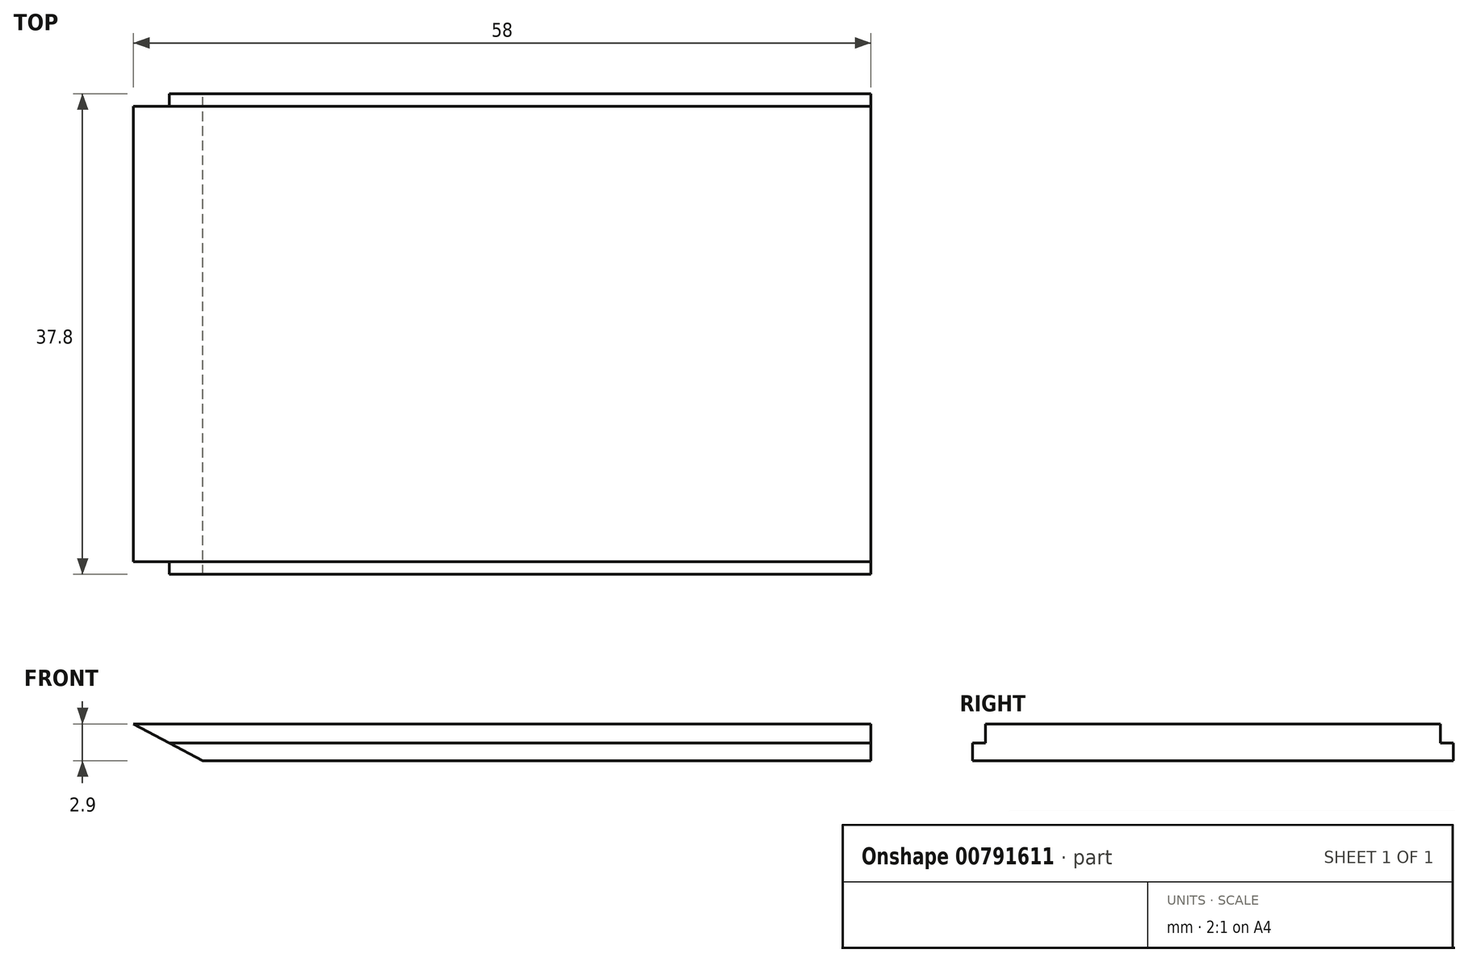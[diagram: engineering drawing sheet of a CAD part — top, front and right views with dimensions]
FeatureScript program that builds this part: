
annotation { "Feature Type Name" : "Feature", "Feature Type Description" : "" }
export const myFeature = defineFeature(function(context is Context, id is Id, definition is map)
    precondition{}
    {
        {
            var Q0;
            Q0=qCreatedBy(makeId("Top.planeOp"),FACE);
            var sketch = newSketch(context, id + "F0", { "sketchPlane" : qUnion([Q0])});
            skLineSegment(sketch, "E0.bottom", {"start": v(29, -18.9) * mm, "end": v(-29, -18.9) * mm});
            skLineSegment(sketch, "E0.top", {"start": v(29, 18.9) * mm, "end": v(-29, 18.9) * mm});
            skLineSegment(sketch, "E0.left", {"start": v(29, -18.9) * mm, "end": v(29, 18.9) * mm});
            skLineSegment(sketch, "E0.right", {"start": v(-29, -18.9) * mm, "end": v(-29, 18.9) * mm});
            skPoint(sketch, "E0.middle", {"position": v(0, 0) * mm});
            skSolve(sketch);
        }
        {
            var Q0;
            Q0 = qSketchRegion(id + "F0", true);
            extrude(context, id + "F1", {"entities" : qUnion([Q0]), "depth" : 1.4 * mm, "offsetDistance" : 25 * mm});
        }
        {
            var Q0;
            Q0=makeQuery(id+"F1.opExtrude","CAP_FACE",FACE,{"disambiguationData":[OSD([sQuery(id+"F0.wireOp",EDGE,"E0.bottom"),sQuery(id+"F0.wireOp",EDGE,"E0.top"),sQuery(id+"F0.wireOp",EDGE,"E0.left"),sQuery(id+"F0.wireOp",EDGE,"E0.right")])],"isStart":false});
            var sketch = newSketch(context, id + "F2", { "sketchPlane" : qUnion([Q0])});
            skLineSegment(sketch, "E1.bottom", {"start": v(29, -17.9) * mm, "end": v(-29, -17.9) * mm});
            skLineSegment(sketch, "E1.top", {"start": v(29, 17.9) * mm, "end": v(-29, 17.9) * mm});
            skLineSegment(sketch, "E1.left", {"start": v(29, -17.9) * mm, "end": v(29, 17.9) * mm});
            skLineSegment(sketch, "E1.right", {"start": v(-29, -17.9) * mm, "end": v(-29, 17.9) * mm});
            skPoint(sketch, "E1.middle", {"position": v(0, 0) * mm});
            skSolve(sketch);
        }
        {
            var Q0;
            Q0 = qSketchRegion(id + "F2", true);
            extrude(context, id + "F3", {"entities" : qUnion([Q0]), "operationType" : NewBodyOperationType.ADD, "depth" : 1.5 * mm, "offsetDistance" : 25 * mm});
        }
        {
            var Q0;
            Q0=makeQuery(id+"F3.opExtrude","SWEPT_FACE",FACE,{"disambiguationData":[OSD([sQuery(id+"F2.wireOp",EDGE,"E1.top")])]});
            var sketch = newSketch(context, id + "F4", { "sketchPlane" : qUnion([Q0])});
            skLineSegment(sketch, "E2", {"start": v(29, 2.9) * mm, "end": v(23.55, 2.9) * mm});
            skLineSegment(sketch, "E3", {"start": v(23.55, 2.9) * mm, "end": v(23.55, 0) * mm});
            skLineSegment(sketch, "E4", {"start": v(23.55, 0) * mm, "end": v(29, 2.9) * mm});
            skSolve(sketch);
        }
        {
            var Q0;
            Q0=makeQuery(id+"F1.opExtrude","SWEPT_FACE",FACE,{"disambiguationData":[OSD([sQuery(id+"F0.wireOp",EDGE,"E0.top")])]});
            var sketch = newSketch(context, id + "F5", { "sketchPlane" : qUnion([Q0])});
            skPoint(sketch, "E5", {"position": v(29, 2.9) * mm});
            skPoint(sketch, "E6", {"position": v(23.55, 0) * mm});
            skPoint(sketch, "E7", {"position": v(23.55, 1.4) * mm});
            skLineSegment(sketch, "E8", {"start": v(23.55, 0) * mm, "end": v(29, 2.9) * mm, "construction": true});
            skLineSegment(sketch, "E9", {"start": v(23.55, 0) * mm, "end": v(23.55, 2.9) * mm, "construction": true});
            skLineSegment(sketch, "E10", {"start": v(23.55, 2.9) * mm, "end": v(29, 2.9) * mm, "construction": true});
            skLineSegment(sketch, "E11", {"start": v(23.55, 1.4) * mm, "end": v(29, 1.4) * mm, "construction": true});
            skPoint(sketch, "E12", {"position": v(26.19, 1.4) * mm});
            skLineSegment(sketch, "E13", {"start": v(26.19, 1.4) * mm, "end": v(23.55, 1.4) * mm});
            skLineSegment(sketch, "E14", {"start": v(23.55, 0) * mm, "end": v(26.19, 1.4) * mm});
            skSolve(sketch);
        }
        {
            var Q0;
            {var subQ1=sQuery(id+"F2.wireOp",EDGE,"E1.top");var subQ2=makeQuery(id+"F3.opExtrude","SWEPT_EDGE",EDGE,{"disambiguationData":[OSD([sQuery(id+"F0.wireOp",EDGE,"E0.right"),subQ1,sQuery(id+"F2.wireOp",EDGE,"E1.right")])]});Q0=makeQuery(id+"F4.imprint","IMPRINT",FACE,{"disambiguationData":[TD([[makeQuery(id+"F4.imprint","IMPRINT",EDGE,{"derivedFrom":subQ2}),-1.0]])]});}
            extrude(context, id + "F6", {"entities" : qUnion([Q0]), "operationType" : NewBodyOperationType.REMOVE, "endBound" : BoundingType.THROUGH_ALL, "oppositeDirection" : true, "depth" : 25 * mm, "offsetDistance" : 25 * mm});
        }
        {
            var Q0;
            {var subQ0=sQuery(id+"F5.wireOp",EDGE,"E14");Q0=makeQuery(id+"F5.imprint","IMPRINT",FACE,{"disambiguationData":[TD([[makeQuery(id+"F5.imprint","IMPRINT",EDGE,{"derivedFrom":subQ0}),-1.0]])]});}
            extrude(context, id + "F7", {"entities" : qUnion([Q0]), "operationType" : NewBodyOperationType.REMOVE, "endBound" : BoundingType.THROUGH_ALL, "oppositeDirection" : true, "depth" : 25 * mm, "offsetDistance" : 25 * mm});
        }
    });
